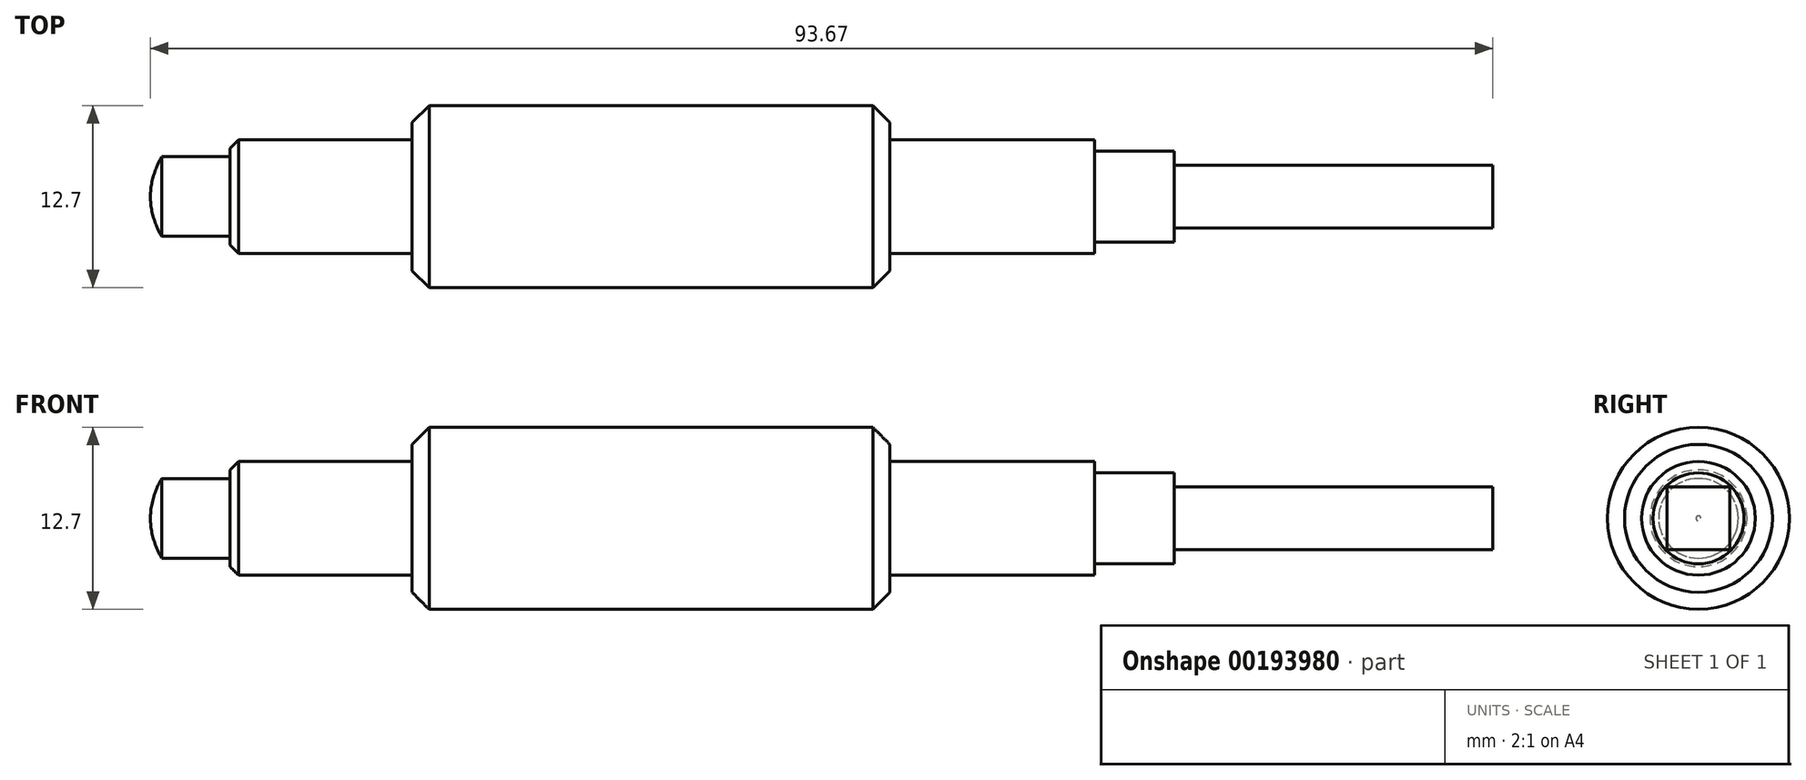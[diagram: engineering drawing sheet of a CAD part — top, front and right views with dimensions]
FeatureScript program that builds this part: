
annotation { "Feature Type Name" : "Feature", "Feature Type Description" : "" }
export const myFeature = defineFeature(function(context is Context, id is Id, definition is map)
    precondition{}
    {
        {
            var Q0;
            Q0=qCreatedBy(makeId("Front.planeOp"),FACE);
            var sketch = newSketch(context, id + "F0", { "sketchPlane" : qUnion([Q0])});
            skLineSegment(sketch, "E0", {"start": v(-35.32, 2.78) * mm, "end": v(-30.56, 2.78) * mm});
            skLineSegment(sketch, "E1", {"start": v(-30.56, 2.78) * mm, "end": v(-30.56, 3.97) * mm});
            skLineSegment(sketch, "E2", {"start": v(-30.56, 3.97) * mm, "end": v(-17.86, 3.97) * mm});
            skLineSegment(sketch, "E3", {"start": v(-17.86, 3.97) * mm, "end": v(-17.86, 6.35) * mm});
            skLineSegment(sketch, "E4", {"start": v(-17.86, 6.35) * mm, "end": v(15.48, 6.35) * mm});
            skLineSegment(sketch, "E5", {"start": v(15.48, 6.35) * mm, "end": v(15.48, 3.97) * mm});
            skLineSegment(sketch, "E6", {"start": v(15.48, 3.97) * mm, "end": v(29.77, 3.97) * mm});
            skLineSegment(sketch, "E7", {"start": v(29.77, 3.97) * mm, "end": v(29.77, 3.17) * mm});
            skLineSegment(sketch, "E8", {"start": v(29.77, 3.17) * mm, "end": v(35.32, 3.17) * mm});
            skLineSegment(sketch, "E9", {"start": v(35.32, 3.17) * mm, "end": v(35.32, 0) * mm});
            skLineSegment(sketch, "E10", {"start": v(35.32, 0) * mm, "end": v(-35.32, 0) * mm});
            skLineSegment(sketch, "E11", {"start": v(-35.32, 2.78) * mm, "end": v(-35.32, 0) * mm, "construction": true});
            skArc(sketch, "E12", {"start": v(-35.32, 2.78) * mm, "mid": v(-35.9, 1.44) * mm, "end": v(-36.12, 0) * mm});
            skLineSegment(sketch, "E13", {"start": v(-35.32, 0) * mm, "end": v(-36.12, 0) * mm});
            skSolve(sketch);
        }
        {
            var Q0;
            Q0=makeQuery(id+"F0.imprint","IMPRINT",FACE,{"disambiguationData":[TD([[makeQuery(id+"F0.imprint","IMPRINT",EDGE,{"derivedFrom":sQuery(id+"F0.wireOp",EDGE,"E0")}),-1.0]])]});
            var Q1;
            Q1=sQuery(id+"F0.wireOp",EDGE,"E10");
            revolve(context, id + "F1", {"entities" : qUnion([Q0]), "axis" : qUnion([Q1]), "revolveType" : RevolveType.FULL});
        }
        {
            var Q0;
            Q0=makeQuery(id+"F1.opRevolve","SWEPT_FACE",FACE,{"disambiguationData":[OSD([sQuery(id+"F0.wireOp",EDGE,"E9")])]});
            var sketch = newSketch(context, id + "F2", { "sketchPlane" : qUnion([Q0])});
            skLineSegment(sketch, "E14.bottom", {"start": v(2.18, -2.18) * mm, "end": v(-2.18, -2.18) * mm});
            skLineSegment(sketch, "E14.top", {"start": v(2.18, 2.18) * mm, "end": v(-2.18, 2.18) * mm});
            skLineSegment(sketch, "E14.left", {"start": v(2.18, -2.18) * mm, "end": v(2.18, 2.18) * mm});
            skLineSegment(sketch, "E14.right", {"start": v(-2.18, -2.18) * mm, "end": v(-2.18, 2.18) * mm});
            skPoint(sketch, "E14.middle", {"position": v(0, 0) * mm});
            skSolve(sketch);
        }
        {
            var Q0;
            Q0=makeQuery(id+"F2.imprint","IMPRINT",FACE,{"disambiguationData":[TD([[makeQuery(id+"F2.imprint","IMPRINT",EDGE,{"derivedFrom":sQuery(id+"F2.wireOp",EDGE,"E14.bottom")}),-1.0]])]});
            extrude(context, id + "F3", {"entities" : qUnion([Q0]), "operationType" : NewBodyOperationType.ADD, "depth" : 22.22 * mm});
        }
        {
            var Q0;
            Q0=makeQuery(id+"F1.opRevolve","SWEPT_EDGE",EDGE,{"disambiguationData":[OSD([sQuery(id+"F0.wireOp",EDGE,"E1"),sQuery(id+"F0.wireOp",EDGE,"E2")])]});
            chamfer(context, id + "F4", {"entities" : qUnion([Q0]), "width" : 0.59 * mm, "tangentPropagation" : true});
        }
        {
            var Q0;
            Q0=makeQuery(id+"F1.opRevolve","SWEPT_EDGE",EDGE,{"disambiguationData":[OSD([sQuery(id+"F0.wireOp",EDGE,"E3"),sQuery(id+"F0.wireOp",EDGE,"E4")])]});
            chamfer(context, id + "F5", {"entities" : qUnion([Q0]), "width" : 1.19 * mm, "tangentPropagation" : true});
        }
        {
            var Q0;
            Q0=makeQuery(id+"F1.opRevolve","SWEPT_EDGE",EDGE,{"disambiguationData":[OSD([sQuery(id+"F0.wireOp",EDGE,"E4"),sQuery(id+"F0.wireOp",EDGE,"E5")])]});
            chamfer(context, id + "F6", {"entities" : qUnion([Q0]), "width" : 1.19 * mm, "tangentPropagation" : true});
        }
    });
